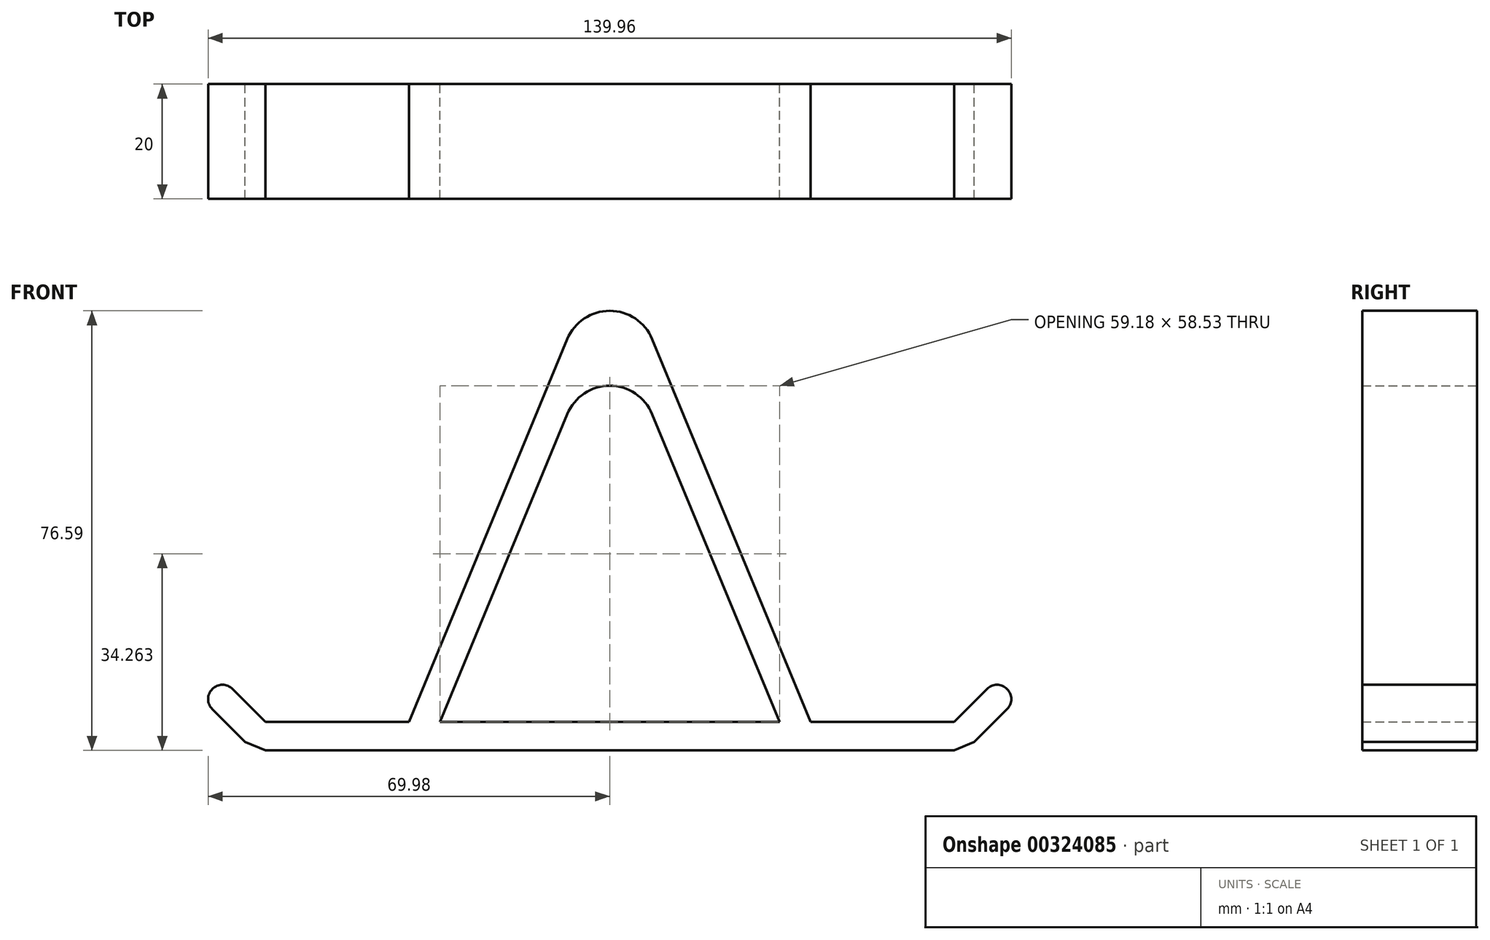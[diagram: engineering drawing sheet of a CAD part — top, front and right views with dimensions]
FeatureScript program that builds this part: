
annotation { "Feature Type Name" : "Feature", "Feature Type Description" : "" }
export const myFeature = defineFeature(function(context is Context, id is Id, definition is map)
    precondition{}
    {
        {
            var Q0;
            Q0=qCreatedBy(makeId("Front.planeOp"),FACE);
            var sketch = newSketch(context, id + "F0", { "sketchPlane" : qUnion([Q0])});
            skLineSegment(sketch, "E0", {"start": v(0, 0) * mm, "end": v(-60, 0) * mm});
            skLineSegment(sketch, "E1.MirrorCS", {"start": v(0, 0) * mm, "end": v(60, 0) * mm});
            skLineSegment(sketch, "E2", {"start": v(-35, 0) * mm, "end": v(0, 84.5) * mm});
            skLineSegment(sketch, "E3", {"start": v(-60, 0) * mm, "end": v(-67.07, 7.07) * mm});
            skLineSegment(sketch, "E4.0", {"start": v(-63.54, -3.54) * mm, "end": v(-71.55, 4.48) * mm});
            skLineSegment(sketch, "E5.0", {"start": v(0, -5) * mm, "end": v(-60, -5) * mm});
            skLineSegment(sketch, "E6.0", {"start": v(-29.59, 0) * mm, "end": v(0, 71.43) * mm});
            skLineSegment(sketch, "E7", {"start": v(0, 84.5) * mm, "end": v(0, 71.43) * mm});
            skLineSegment(sketch, "E8", {"start": v(-67.07, 7.07) * mm, "end": v(-71.55, 4.48) * mm});
            skLineSegment(sketch, "E9", {"start": v(-63.54, -3.54) * mm, "end": v(-60, -5) * mm});
            skLineSegment(sketch, "E10", {"start": v(0, -5) * mm, "end": v(0, 0) * mm});
            skLineSegment(sketch, "E11.MirrorCS", {"start": v(35, 0) * mm, "end": v(0, 84.5) * mm});
            skLineSegment(sketch, "E12.MirrorCS", {"start": v(29.59, 0) * mm, "end": v(0, 71.43) * mm});
            skLineSegment(sketch, "E13.MirrorCS", {"start": v(0, -5) * mm, "end": v(60, -5) * mm});
            skLineSegment(sketch, "E14.MirrorCS", {"start": v(63.54, -3.54) * mm, "end": v(60, -5) * mm});
            skLineSegment(sketch, "E15.MirrorCS", {"start": v(63.54, -3.54) * mm, "end": v(71.55, 4.48) * mm});
            skLineSegment(sketch, "E16.MirrorCS", {"start": v(67.07, 7.07) * mm, "end": v(71.55, 4.48) * mm});
            skLineSegment(sketch, "E17.MirrorCS", {"start": v(60, 0) * mm, "end": v(67.07, 7.07) * mm});
            skSolve(sketch);
        }
        {
            var Q0;
            {var subQ0=sQuery(id+"F0.wireOp",EDGE,"E2");Q0=makeQuery(id+"F0.imprint","IMPRINT",FACE,{"disambiguationData":[TD([[makeQuery(id+"F0.imprint","IMPRINT",EDGE,{"derivedFrom":subQ0}),-1.0]])]});}
            var Q1;
            Q1=makeQuery(id+"F0.imprint","IMPRINT",FACE,{"disambiguationData":[TD([[makeQuery(id+"F0.imprint","IMPRINT",EDGE,{"derivedFrom":sQuery(id+"F0.wireOp",EDGE,"E7")}),1.0]])]});
            var Q2;
            {var subQ0=sQuery(id+"F0.wireOp",EDGE,"E3");Q2=makeQuery(id+"F0.imprint","IMPRINT",FACE,{"disambiguationData":[TD([[makeQuery(id+"F0.imprint","IMPRINT",EDGE,{"derivedFrom":subQ0}),1.0]])]});}
            var Q3;
            {var subQ3=sQuery(id+"F0.wireOp",EDGE,"E10");Q3=makeQuery(id+"F0.imprint","IMPRINT",FACE,{"disambiguationData":[TD([[makeQuery(id+"F0.imprint","IMPRINT",EDGE,{"derivedFrom":subQ3}),-1.0]])]});}
            extrude(context, id + "F1", {"entities" : qUnion([Q0, Q1, Q2, Q3]), "depth" : 20 * mm});
        }
        {
            var Q0;
            Q0=makeQuery(id+"F1.opExtrude","SWEPT_EDGE",EDGE,{"disambiguationData":[OSD([sQuery(id+"F0.wireOp",EDGE,"E2"),sQuery(id+"F0.wireOp",EDGE,"E7"),sQuery(id+"F0.wireOp",EDGE,"E11.MirrorCS")])]});
            var Q1;
            Q1=makeQuery(id+"F1.opExtrude","SWEPT_EDGE",EDGE,{"disambiguationData":[OSD([sQuery(id+"F0.wireOp",EDGE,"E6.0"),sQuery(id+"F0.wireOp",EDGE,"E7"),sQuery(id+"F0.wireOp",EDGE,"E12.MirrorCS")])]});
            fillet(context, id + "F2", {"entities" : qUnion([Q0, Q1]), "radius" : 8 * mm, "tangentPropagation" : true, "allowEdgeOverflow" : false});
        }
        {
            var Q0;
            Q0=makeQuery(id+"F1.opExtrude","SWEPT_EDGE",EDGE,{"disambiguationData":[OSD([sQuery(id+"F0.wireOp",EDGE,"E3"),sQuery(id+"F0.wireOp",EDGE,"E8")])]});
            var Q1;
            Q1=makeQuery(id+"F1.opExtrude","SWEPT_EDGE",EDGE,{"disambiguationData":[OSD([sQuery(id+"F0.wireOp",EDGE,"E4.0"),sQuery(id+"F0.wireOp",EDGE,"E8")])]});
            var Q2;
            Q2=makeQuery(id+"F1.opExtrude","SWEPT_EDGE",EDGE,{"disambiguationData":[OSD([sQuery(id+"F0.wireOp",EDGE,"E16.MirrorCS"),sQuery(id+"F0.wireOp",EDGE,"E17.MirrorCS")])]});
            var Q3;
            Q3=makeQuery(id+"F1.opExtrude","SWEPT_EDGE",EDGE,{"disambiguationData":[OSD([sQuery(id+"F0.wireOp",EDGE,"E15.MirrorCS"),sQuery(id+"F0.wireOp",EDGE,"E16.MirrorCS")])]});
            fillet(context, id + "F3", {"entities" : qUnion([Q0, Q1, Q2, Q3]), "radius" : 2.5 * mm, "tangentPropagation" : true, "allowEdgeOverflow" : false});
        }
    });
